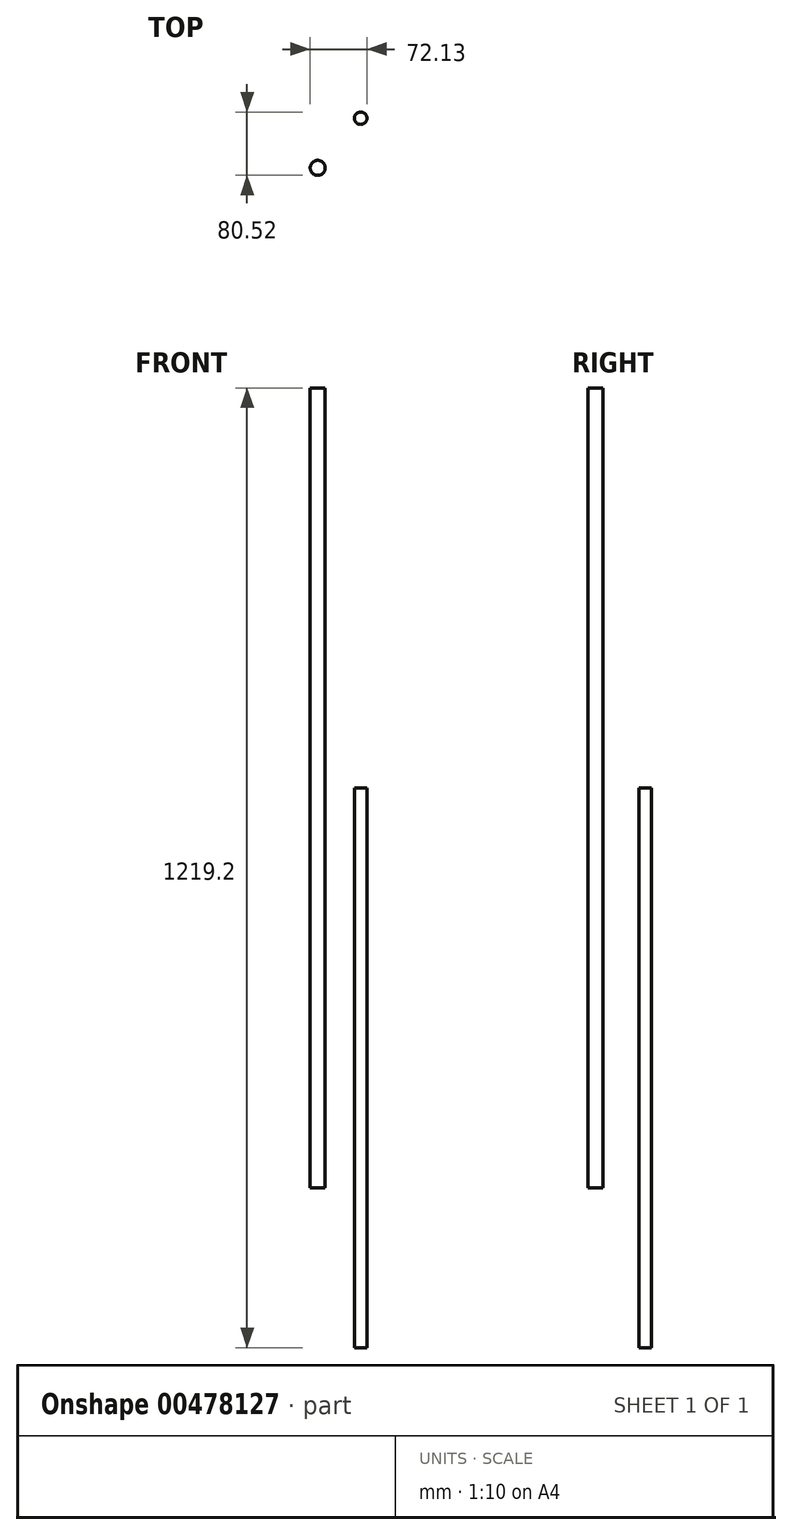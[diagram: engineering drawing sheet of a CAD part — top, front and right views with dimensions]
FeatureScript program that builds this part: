
annotation { "Feature Type Name" : "Feature", "Feature Type Description" : "" }
export const myFeature = defineFeature(function(context is Context, id is Id, definition is map)
    precondition{}
    {
        {
            var Q0;
            Q0=qCreatedBy(makeId("Top.planeOp"),FACE);
            var sketch = newSketch(context, id + "F0", { "sketchPlane" : qUnion([Q0])});
            skCircle(sketch, "E0", {"center": v(0, 0) * mm, "radius": 7.94 * mm});
            skSolve(sketch);
        }
        {
            var Q0;
            Q0=makeQuery(id+"F0.imprint","IMPRINT",FACE,{"disambiguationData":[TD([[makeQuery(id+"F0.imprint","IMPRINT",EDGE,{"derivedFrom":sQuery(id+"F0.wireOp",EDGE,"E0")}),1.0]])]});
            extrude(context, id + "F1", {"entities" : qUnion([Q0]), "depth" : 355.6 * mm, "offsetDistance" : 25.4 * mm, "hasSecondDirection" : true, "secondDirectionOppositeDirection" : true, "secondDirectionDepth" : 355.6 * mm});
        }
        {
            var Q0;
            Q0=qCreatedBy(makeId("Top.planeOp"),FACE);
            var sketch = newSketch(context, id + "F2", { "sketchPlane" : qUnion([Q0])});
            skCircle(sketch, "E1", {"center": v(-54.66, -63.06) * mm, "radius": 9.53 * mm});
            skSolve(sketch);
        }
        {
            var Q0;
            Q0=makeQuery(id+"F2.imprint","IMPRINT",FACE,{"disambiguationData":[TD([[makeQuery(id+"F2.imprint","IMPRINT",EDGE,{"derivedFrom":sQuery(id+"F2.wireOp",EDGE,"E1")}),1.0]])]});
            extrude(context, id + "F3", {"entities" : qUnion([Q0]), "depth" : 863.6 * mm, "offsetDistance" : 25.4 * mm, "hasSecondDirection" : true, "secondDirectionOppositeDirection" : true, "secondDirectionDepth" : 152.4 * mm});
        }
    });
